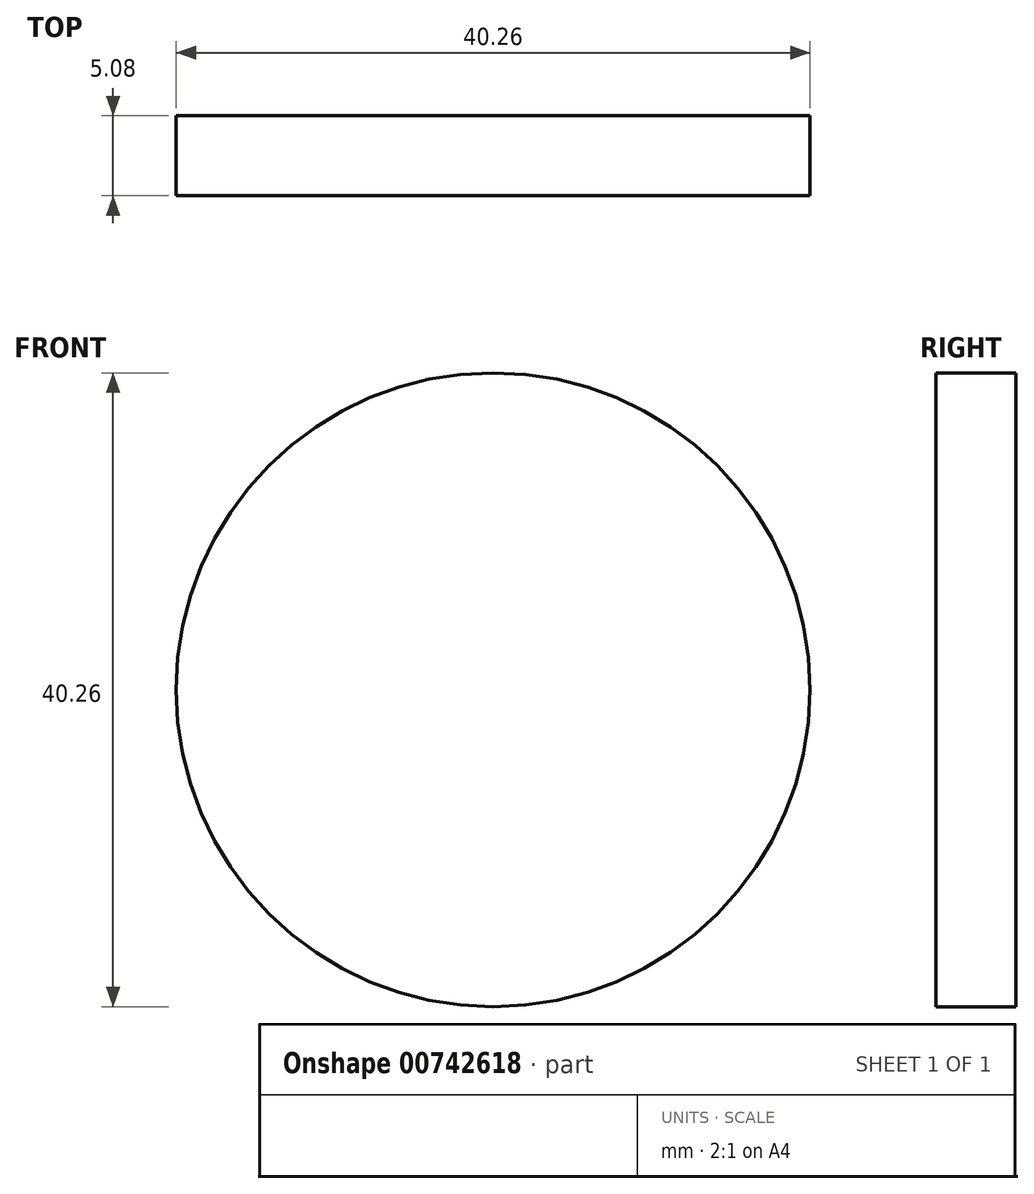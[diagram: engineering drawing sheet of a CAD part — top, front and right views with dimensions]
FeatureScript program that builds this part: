
annotation { "Feature Type Name" : "Feature", "Feature Type Description" : "" }
export const myFeature = defineFeature(function(context is Context, id is Id, definition is map)
    precondition{}
    {
        {
            var Q0;
            Q0=qCreatedBy(makeId("Front.planeOp"),FACE);
            var sketch = newSketch(context, id + "F0", { "sketchPlane" : qUnion([Q0])});
            skCircle(sketch, "E0", {"center": v(0, 0) * mm, "radius": 20.13 * mm});
            skSolve(sketch);
        }
        {
            var Q0;
            Q0 = qSketchRegion(id + "F0", true);
            extrude(context, id + "F1", {"entities" : qUnion([Q0]), "depth" : 5.08 * mm, "offsetDistance" : 25.4 * mm});
        }
    });
